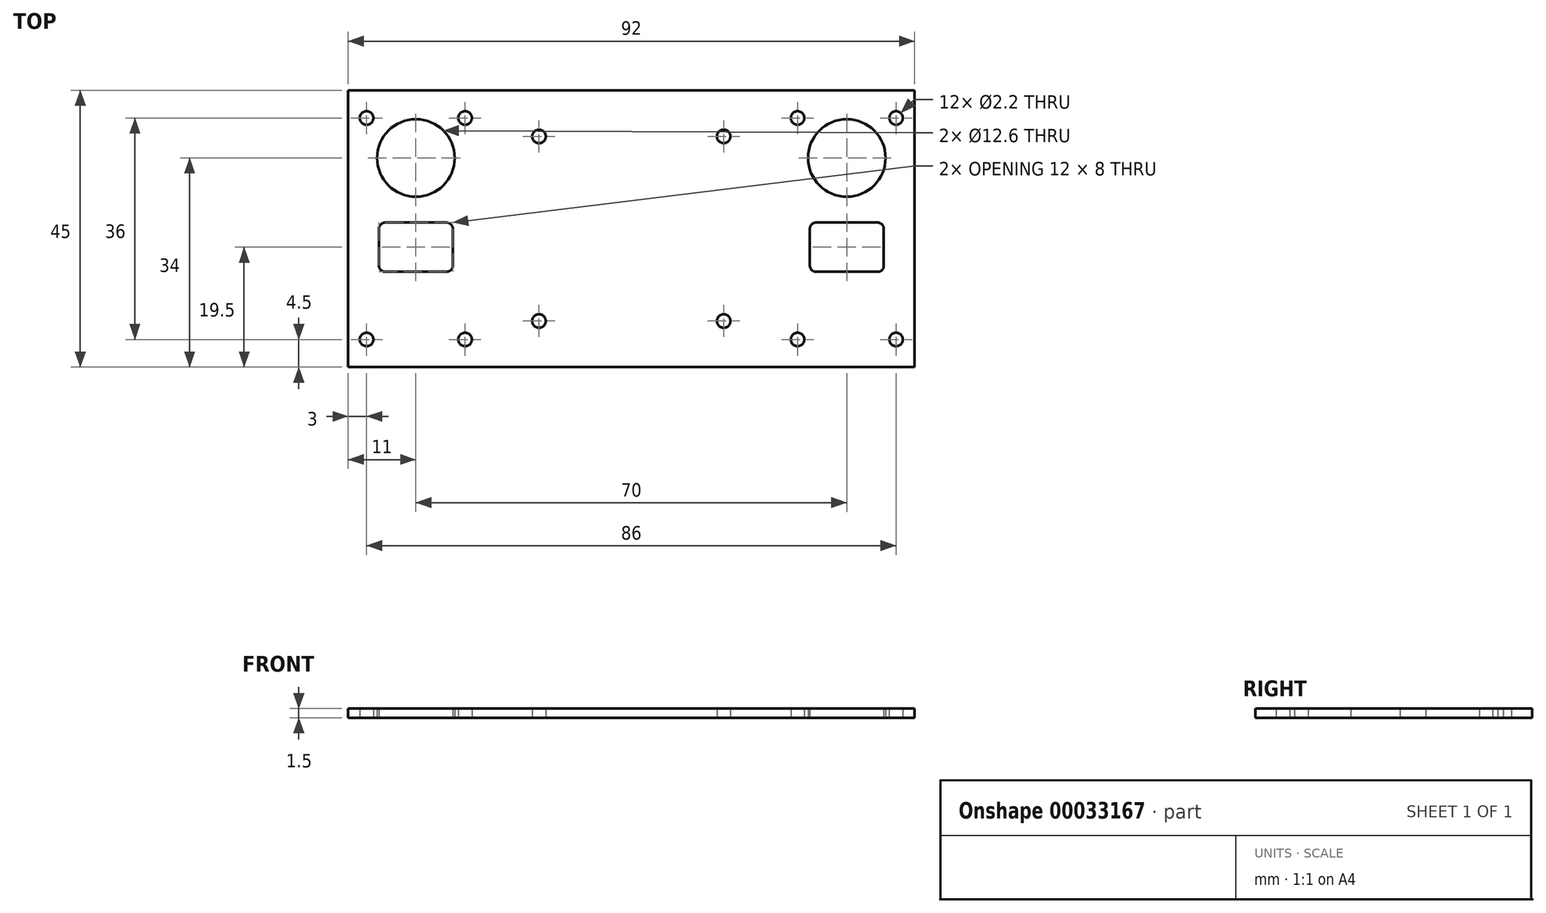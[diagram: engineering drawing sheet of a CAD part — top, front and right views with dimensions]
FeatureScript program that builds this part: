
annotation { "Feature Type Name" : "Feature", "Feature Type Description" : "" }
export const myFeature = defineFeature(function(context is Context, id is Id, definition is map)
    precondition{}
    {
        {
            var Q0;
            Q0=qCreatedBy(makeId("Top.planeOp"),FACE);
            var sketch = newSketch(context, id + "F0", { "sketchPlane" : qUnion([Q0])});
            skLineSegment(sketch, "E0.bottom", {"start": v(-46, 22.5) * mm, "end": v(46, 22.5) * mm});
            skLineSegment(sketch, "E0.top", {"start": v(-46, -22.5) * mm, "end": v(46, -22.5) * mm});
            skLineSegment(sketch, "E0.left", {"start": v(-46, 22.5) * mm, "end": v(-46, -22.5) * mm});
            skLineSegment(sketch, "E0.right", {"start": v(46, 22.5) * mm, "end": v(46, -22.5) * mm});
            skPoint(sketch, "E0.middle", {"position": v(0, 0) * mm});
            skLineSegment(sketch, "E1", {"start": v(-35, 22.5) * mm, "end": v(-35, -22.5) * mm, "construction": true});
            skCircle(sketch, "E2", {"center": v(-43, 18) * mm, "radius": 1.1 * mm});
            skCircle(sketch, "E3", {"center": v(-43, -18) * mm, "radius": 1.1 * mm});
            skCircle(sketch, "E4.MirrorC", {"center": v(-27, 18) * mm, "radius": 1.1 * mm});
            skCircle(sketch, "E5.MirrorC", {"center": v(-27, -18) * mm, "radius": 1.1 * mm});
            skCircle(sketch, "E6", {"center": v(-35, 11.5) * mm, "radius": 6.3 * mm});
            skCircle(sketch, "E7.MirrorC", {"center": v(27, -18) * mm, "radius": 1.1 * mm});
            skCircle(sketch, "E8.MirrorC", {"center": v(35, 11.5) * mm, "radius": 6.3 * mm});
            skCircle(sketch, "E9.MirrorC", {"center": v(27, 18) * mm, "radius": 1.1 * mm});
            skCircle(sketch, "E10.MirrorC", {"center": v(43, 18) * mm, "radius": 1.1 * mm});
            skCircle(sketch, "E11.MirrorC", {"center": v(43, -18) * mm, "radius": 1.1 * mm});
            skLineSegment(sketch, "E12.bottom", {"start": v(-15, 15) * mm, "end": v(15, 15) * mm, "construction": true});
            skLineSegment(sketch, "E12.top", {"start": v(-15, -15) * mm, "end": v(15, -15) * mm, "construction": true});
            skLineSegment(sketch, "E12.left", {"start": v(-15, 15) * mm, "end": v(-15, -15) * mm, "construction": true});
            skLineSegment(sketch, "E12.right", {"start": v(15, 15) * mm, "end": v(15, -15) * mm, "construction": true});
            skCircle(sketch, "E13", {"center": v(-15, 15) * mm, "radius": 1.1 * mm});
            skCircle(sketch, "E14", {"center": v(-15, -15) * mm, "radius": 1.1 * mm});
            skCircle(sketch, "E15.MirrorC", {"center": v(15, 15) * mm, "radius": 1.1 * mm});
            skCircle(sketch, "E16.MirrorC", {"center": v(15, -15) * mm, "radius": 1.1 * mm});
            skCircle(sketch, "E17", {"center": v(0, 0) * mm, "radius": 10 * mm, "construction": true});
            skLineSegment(sketch, "E18.bottom", {"start": v(-30, -7) * mm, "end": v(-40, -7) * mm});
            skLineSegment(sketch, "E18.top", {"start": v(-30, 1) * mm, "end": v(-40, 1) * mm});
            skLineSegment(sketch, "E18.left", {"start": v(-29, -6) * mm, "end": v(-29, 0) * mm});
            skLineSegment(sketch, "E18.right", {"start": v(-41, -6) * mm, "end": v(-41, 0) * mm});
            skPoint(sketch, "E18.middle", {"position": v(-35, -3) * mm});
            skPoint(sketch, "E19.visualSharp", {"position": v(-41, 1) * mm});
            skArc(sketch, "E19.filletArc", {"start": v(-40, 1) * mm, "mid": v(-40.7, 0.7) * mm, "end": v(-41, 0) * mm});
            skPoint(sketch, "E20.visualSharp", {"position": v(-41, -7) * mm});
            skArc(sketch, "E20.filletArc", {"start": v(-41, -6) * mm, "mid": v(-40.7, -6.7) * mm, "end": v(-40, -7) * mm});
            skPoint(sketch, "E21.visualSharp", {"position": v(-29, -7) * mm});
            skArc(sketch, "E21.filletArc", {"start": v(-30, -7) * mm, "mid": v(-29.3, -6.7) * mm, "end": v(-29, -6) * mm});
            skPoint(sketch, "E22.visualSharp", {"position": v(-29, 1) * mm});
            skArc(sketch, "E22.filletArc", {"start": v(-29, 0) * mm, "mid": v(-29.3, 0.7) * mm, "end": v(-30, 1) * mm});
            skArc(sketch, "E23.MirrorCS", {"start": v(40, 1) * mm, "mid": v(40.7, 0.7) * mm, "end": v(41, 0) * mm});
            skArc(sketch, "E24.MirrorCS", {"start": v(30, -7) * mm, "mid": v(29.3, -6.7) * mm, "end": v(29, -6) * mm});
            skArc(sketch, "E25.MirrorCS", {"start": v(29, 0) * mm, "mid": v(29.3, 0.7) * mm, "end": v(30, 1) * mm});
            skArc(sketch, "E26.MirrorCS", {"start": v(41, -6) * mm, "mid": v(40.7, -6.7) * mm, "end": v(40, -7) * mm});
            skLineSegment(sketch, "E27.MirrorCS", {"start": v(41, -6) * mm, "end": v(41, 0) * mm});
            skLineSegment(sketch, "E28.MirrorCS", {"start": v(30, -7) * mm, "end": v(40, -7) * mm});
            skPoint(sketch, "E29.MirrorP", {"position": v(29, -7) * mm});
            skPoint(sketch, "E30.MirrorP", {"position": v(41, -7) * mm});
            skPoint(sketch, "E31.MirrorP", {"position": v(41, 1) * mm});
            skPoint(sketch, "E32.MirrorP", {"position": v(35, -3) * mm});
            skLineSegment(sketch, "E33.MirrorCS", {"start": v(30, 1) * mm, "end": v(40, 1) * mm});
            skLineSegment(sketch, "E34.MirrorCS", {"start": v(29, -6) * mm, "end": v(29, 0) * mm});
            skPoint(sketch, "E35.MirrorP", {"position": v(29, 1) * mm});
            skSolve(sketch);
        }
        {
            var Q0;
            Q0 = qSketchRegion(id + "F0", true);
            extrude(context, id + "F1", {"entities" : qUnion([Q0]), "depth" : 1.5 * mm});
        }
    });
